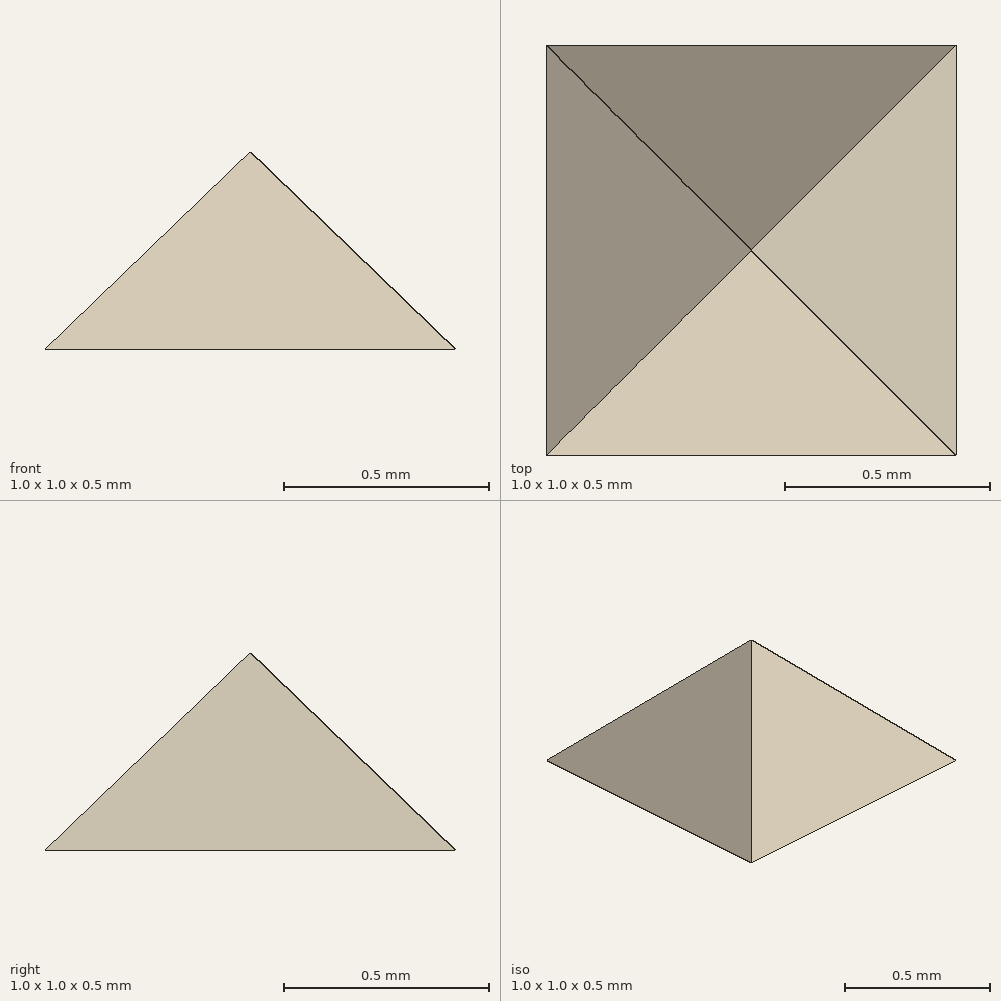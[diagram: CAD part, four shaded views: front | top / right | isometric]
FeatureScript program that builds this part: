
annotation { "Feature Type Name" : "Feature", "Feature Type Description" : "" }
export const myFeature = defineFeature(function(context is Context, id is Id, definition is map)
    precondition{}
    {
        {
            var Q0;
            Q0=qCreatedBy(makeId("Top.planeOp"),FACE);
            var sketch = newSketch(context, id + "F0", { "sketchPlane" : qUnion([Q0])});
            skLineSegment(sketch, "E0.bottom", {"start": v(0, 0) * mm, "end": v(1, 0) * mm});
            skLineSegment(sketch, "E0.top", {"start": v(0, -1) * mm, "end": v(1, -1) * mm});
            skLineSegment(sketch, "E0.left", {"start": v(0, 0) * mm, "end": v(0, -1) * mm});
            skLineSegment(sketch, "E0.right", {"start": v(1, 0) * mm, "end": v(1, -1) * mm});
            skSolve(sketch);
        }
        {
            var Q0;
            Q0=makeQuery(id+"F0.imprint","IMPRINT",FACE,{"disambiguationData":[TD([[makeQuery(id+"F0.imprint","IMPRINT",EDGE,{"derivedFrom":sQuery(id+"F0.wireOp",EDGE,"E0.bottom")}),-1.0]])]});
            extrude(context, id + "F1", {"entities" : qUnion([Q0]), "depth" : 2 * mm, "offsetDistance" : 25 * mm});
        }
        {
            var Q0;
            Q0=makeQuery(id+"F1.opExtrude","SWEPT_FACE",FACE,{"disambiguationData":[OSD([sQuery(id+"F0.wireOp",EDGE,"E0.right")])]});
            var sketch = newSketch(context, id + "F2", { "sketchPlane" : qUnion([Q0])});
            skLineSegment(sketch, "E1", {"start": v(-1, 0) * mm, "end": v(-0.5, 0.48) * mm});
            skLineSegment(sketch, "E2", {"start": v(0, 0) * mm, "end": v(-0.5, 0.48) * mm});
            skSolve(sketch);
        }
        {
            var Q0;
            Q0=makeQuery(id+"F1.opExtrude","SWEPT_FACE",FACE,{"disambiguationData":[OSD([sQuery(id+"F0.wireOp",EDGE,"E0.top")])]});
            var sketch = newSketch(context, id + "F3", { "sketchPlane" : qUnion([Q0])});
            skLineSegment(sketch, "E3", {"start": v(0, 0) * mm, "end": v(0.5, 0.48) * mm});
            skLineSegment(sketch, "E4", {"start": v(1, 0) * mm, "end": v(0.5, 0.48) * mm});
            skSolve(sketch);
        }
        {
            var Q0;
            Q0=makeQuery(id+"F3.imprint","IMPRINT",FACE,{"disambiguationData":[TD([[makeQuery(id+"F3.imprint","IMPRINT",EDGE,{"derivedFrom":sQuery(id+"F3.wireOp",EDGE,"E3")}),1.0]])]});
            extrude(context, id + "F4", {"entities" : qUnion([Q0]), "operationType" : NewBodyOperationType.REMOVE, "oppositeDirection" : true, "depth" : 25 * mm, "offsetDistance" : 25 * mm});
        }
        {
            var Q0;
            Q0=makeQuery(id+"F2.imprint","IMPRINT",FACE,{"disambiguationData":[TD([[makeQuery(id+"F2.imprint","IMPRINT",EDGE,{"derivedFrom":sQuery(id+"F2.wireOp",EDGE,"E1")}),1.0]])]});
            extrude(context, id + "F5", {"entities" : qUnion([Q0]), "operationType" : NewBodyOperationType.REMOVE, "oppositeDirection" : true, "depth" : 25 * mm, "offsetDistance" : 25 * mm});
        }
    });
